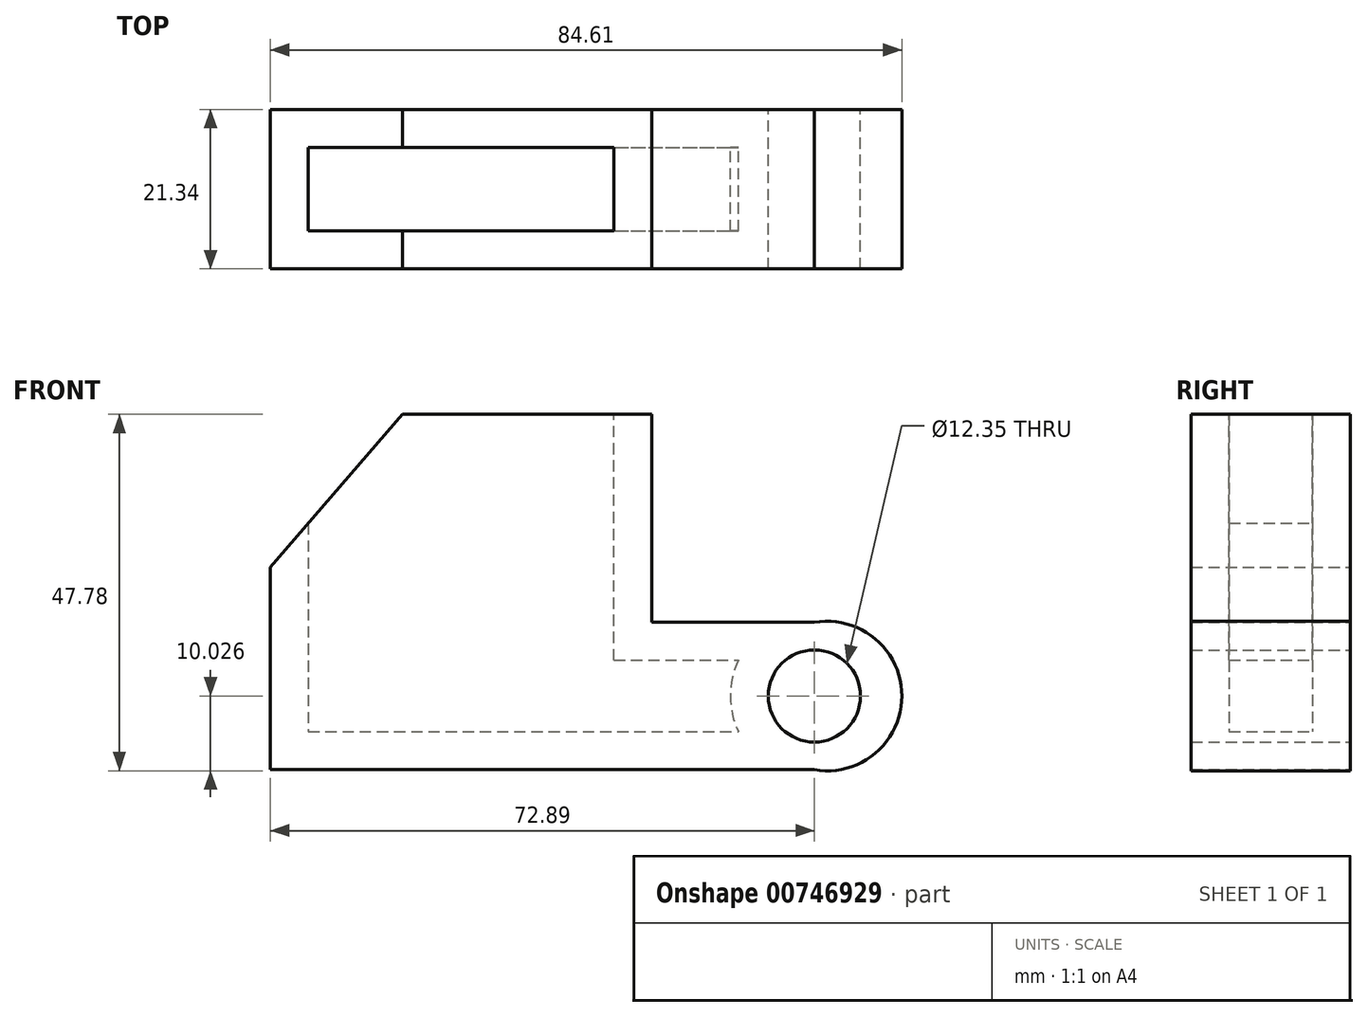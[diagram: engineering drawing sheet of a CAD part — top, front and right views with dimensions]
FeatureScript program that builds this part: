
annotation { "Feature Type Name" : "Feature", "Feature Type Description" : "" }
export const myFeature = defineFeature(function(context is Context, id is Id, definition is map)
    precondition{}
    {
        {
            var Q0;
            Q0=qCreatedBy(makeId("Front.planeOp"),FACE);
            var sketch = newSketch(context, id + "F0", { "sketchPlane" : qUnion([Q0])});
            skLineSegment(sketch, "E0", {"start": v(23.67, 0) * mm, "end": v(23.67, 27.88) * mm});
            skLineSegment(sketch, "E1", {"start": v(23.67, 27.88) * mm, "end": v(0, 27.88) * mm});
            skLineSegment(sketch, "E2", {"start": v(0, 27.88) * mm, "end": v(-9.73, 27.88) * mm});
            skLineSegment(sketch, "E3", {"start": v(-9.73, 27.88) * mm, "end": v(-27.44, 7.4) * mm});
            skLineSegment(sketch, "E4", {"start": v(-27.44, 7.4) * mm, "end": v(-27.44, -19.76) * mm});
            skLineSegment(sketch, "E5", {"start": v(-27.44, -19.76) * mm, "end": v(45.45, -19.76) * mm});
            skLineSegment(sketch, "E6", {"start": v(23.67, 0) * mm, "end": v(45.45, 0) * mm});
            skArc(sketch, "E7", {"start": v(45.45, -19.76) * mm, "mid": v(57.17, -9.88) * mm, "end": v(45.45, 0) * mm});
            skCircle(sketch, "E8", {"center": v(45.45, -9.87) * mm, "radius": 6.17 * mm});
            skLineSegment(sketch, "E9", {"start": v(-16.49, 20.07) * mm, "end": v(-16.49, -19.76) * mm});
            skLineSegment(sketch, "E10", {"start": v(0, 27.88) * mm, "end": v(0, -19.76) * mm});
            skSolve(sketch);
        }
        {
            var Q0;
            {var subQ0=sQuery(id+"F0.wireOp",EDGE,"E4");Q0=makeQuery(id+"F0.imprint","IMPRINT",FACE,{"disambiguationData":[TD([[makeQuery(id+"F0.imprint","IMPRINT",EDGE,{"derivedFrom":subQ0}),1.0]])]});}
            var Q1;
            Q1=makeQuery(id+"F0.imprint","IMPRINT",FACE,{"disambiguationData":[TD([[makeQuery(id+"F0.imprint","IMPRINT",EDGE,{"derivedFrom":sQuery(id+"F0.wireOp",EDGE,"E0")}),1.0]])]});
            var Q2;
            {var subQ1=sQuery(id+"F0.wireOp",EDGE,"E2");Q2=makeQuery(id+"F0.imprint","IMPRINT",FACE,{"disambiguationData":[TD([[makeQuery(id+"F0.imprint","IMPRINT",EDGE,{"derivedFrom":subQ1}),1.0]])]});}
            extrude(context, id + "F1", {"entities" : qUnion([Q0, Q1, Q2]), "depth" : 21.34 * mm, "offsetDistance" : 25.4 * mm});
        }
        {
            var Q0;
            Q0=makeQuery(id+"F1.opExtrude","SWEPT_FACE",FACE,{"disambiguationData":[OSD([sQuery(id+"F0.wireOp",EDGE,"E3")])]});
            var Q1;
            Q1=makeQuery(id+"F1.opExtrude","SWEPT_FACE",FACE,{"disambiguationData":[OSD([sQuery(id+"F0.wireOp",EDGE,"E1"),sQuery(id+"F0.wireOp",EDGE,"E2")])]});
            shell(context, id + "F2", {"entities" : qUnion([Q0, Q1]), "thickness" : 5.08 * mm});
        }
    });
